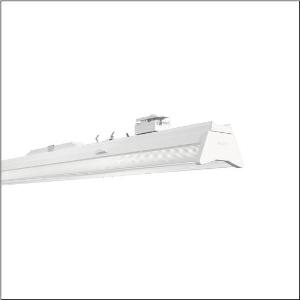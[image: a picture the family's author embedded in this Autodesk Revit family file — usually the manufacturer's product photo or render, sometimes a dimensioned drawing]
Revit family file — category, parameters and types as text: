
# Revit family: licross_r__21_performance_mo_52tm16cn49xg_ab5a
name_source: partatom
category: Lighting Fixtures
units: mm (PartAtom-declared; Revit-internal decimal feet)

## family parameters
Cut with Voids When Loaded = No
Host = Face
Light Source = No
Part Type = Normal
Room Calculation Point = No
Round Connector Dimension = Use Diameter
Shared = No

## types (1)
- --- (1 x LED, 9240 lm, 50.4 W, 4000K)
    Apparent Load = 50 VA
    CIE Flux Codes = 66 88 96 79 100
    Color Rendering = 80
    Color Temperature = 4000K
    Default Elevation = 1800 mm
    Description = Licross® 21 Performance MO, luminaire insert, of sheet steel, galvanised, coil coated, white, length: 1.500mm, width: 120mm, height: 123mm, LED rated luminous flux: 9.240lm, light colour: 840, control gear: ON/OFF Multilumen, CLOi, control gear: ECG Multilumen, with plug, 3-pole, with phase selection, mains connection: 220..240V, AC, 50/60Hz, start of lifetime: 50W, end of service life: 61W, halogen-free wiring, primary light control with lens, of plastic, primary optical cover: cover, of PMMA, light emission: direct/indirect distribution, primary light characteristic: symmetric, protection rating (complete): IP40, insulation class (complete): insulation class I (protective earthing), certification: CE, ENEC, UKCA, protection symbol: D if used in an environment without relevant dust loads with corresponding accessories, impact resistance: IK06, permissible ambient temperature for indoor applications: -35..+45°C, corresponds to IFS (International Featured Standards) requirements for safety and quality in the food industry, reducing of maximum allowable ambient temperature of 5°C with ceiling mounting, LABS conformity tested according to VDMA 24364:2018-05, packaging unit: 1 piece
    Height = 114 mm
    Lamp = 1 x LED
    Lamp Light Flux = 9240 lm
    Lamp Power = 50.4 W
    Lamp count = 1
    Length = 1500 mm
    Luminous efficacy = 183 lm/W
    Manufacturer = Siteco
    ModVariant = No
    Model = 52TM16CN49XG
    Mounting Place = Ceiling
    Mounting Type = Pendant
    Number of Poles = 1
    OnlyDefault = Yes
    Power Factor = 1
    Product Name = Licross® 21 Performance MO
    Product group = luminaire insert
    ProductGroupID = 901
    Protection Class = Protection class I
    Protection Degree = IP 40
    RLX_Detail_Level = 1
    RLX_Emergency_Light_Flux = 0 lm
    RLX_Emergency_Type = 0
    RLX_Emergency_Type_DB = No
    RlxData = <blob elided: 31853 chars, md5=73e034fe>
    Socket = socket
    Standby Power = 0 W
    System Light Flux = 9240 lm
    System Power = 50 W
    Type Comments = factory setting: luminous flux: 100 % | (A | C | E) | 117 mA
    Type Image = l_1256138.jpg
    URL = http://relux.com
    VarID = @adj_041681
    Voltage = 0 V
    Weight = 0.00 kg
    Width = 120 mm

## geometry (parser evidence)
native form markers: Blend x4, Sweep x11
no freeform markers — native parametric forms only
